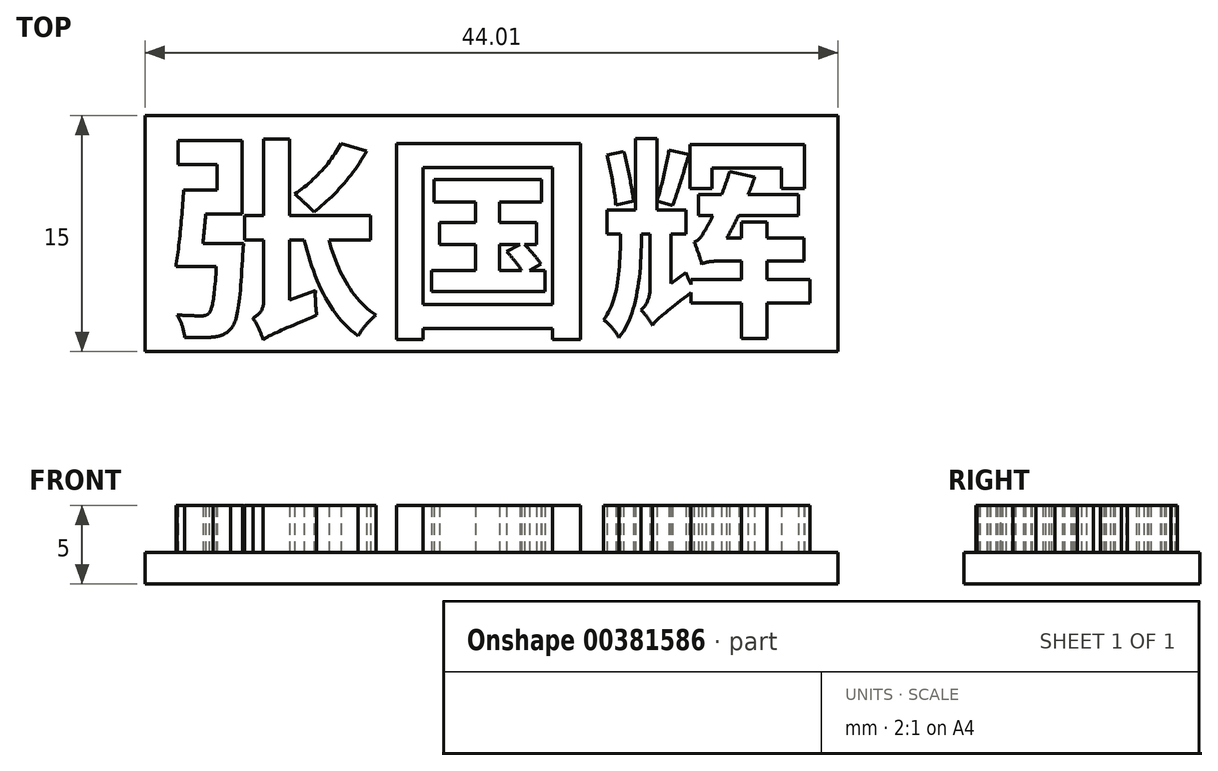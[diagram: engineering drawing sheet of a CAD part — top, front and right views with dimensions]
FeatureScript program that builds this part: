
annotation { "Feature Type Name" : "Feature", "Feature Type Description" : "" }
export const myFeature = defineFeature(function(context is Context, id is Id, definition is map)
    precondition{}
    {
        {
            var Q0;
            Q0=qCreatedBy(makeId("Top.planeOp"),FACE);
            var sketch = newSketch(context, id + "F0", { "sketchPlane" : qUnion([Q0])});
            skText(sketch, "E0", { "text": "张国辉", "fontName": "NotoSansCJKsc-Bold.otf"});
            skLineSegment(sketch, "E1.bottom", {"start": v(-1, 13) * mm, "end": v(43, 13) * mm});
            skLineSegment(sketch, "E1.top", {"start": v(-1, -2) * mm, "end": v(43, -2) * mm});
            skLineSegment(sketch, "E1.left", {"start": v(-1, 13) * mm, "end": v(-1, -2) * mm});
            skLineSegment(sketch, "E1.right", {"start": v(43, 13) * mm, "end": v(43, -2) * mm});
            const initialGuessF0  = {"E0": [0, 0, 1, 0, 0.01]};
            skSetInitialGuess(sketch, initialGuessF0);
            skSolve(sketch);
        }
        {
            var Q0;
            Q0=makeQuery(id+"F0.imprint","IMPRINT",FACE,{"disambiguationData":[TD([[makeQuery(id+"F0.imprint","IMPRINT",EDGE,{"derivedFrom":sQuery(id+"F0.wireOp",EDGE,"E0.sketch_text.stroke-0")}),-1.0]])]});
            var Q1;
            Q1=makeQuery(id+"F0.imprint","IMPRINT",FACE,{"disambiguationData":[TD([[makeQuery(id+"F0.imprint","IMPRINT",EDGE,{"derivedFrom":sQuery(id+"F0.wireOp",EDGE,"E0.sketch_text.stroke-0")}),1.0]])]});
            var Q2;
            Q2=makeQuery(id+"F0.imprint","IMPRINT",FACE,{"disambiguationData":[TD([[makeQuery(id+"F0.imprint","IMPRINT",EDGE,{"derivedFrom":sQuery(id+"F0.wireOp",EDGE,"E0.sketch_text.stroke-19")}),1.0]])]});
            var Q3;
            Q3=makeQuery(id+"F0.imprint","IMPRINT",FACE,{"disambiguationData":[TD([[makeQuery(id+"F0.imprint","IMPRINT",EDGE,{"derivedFrom":sQuery(id+"F0.wireOp",EDGE,"E0.sketch_text.stroke-45")}),1.0]])]});
            var Q4;
            Q4=makeQuery(id+"F0.imprint","IMPRINT",FACE,{"disambiguationData":[TD([[makeQuery(id+"F0.imprint","IMPRINT",EDGE,{"derivedFrom":sQuery(id+"F0.wireOp",EDGE,"E0.sketch_text.stroke-41")}),1.0]])]});
            var Q5;
            Q5=makeQuery(id+"F0.imprint","IMPRINT",FACE,{"disambiguationData":[TD([[makeQuery(id+"F0.imprint","IMPRINT",EDGE,{"derivedFrom":sQuery(id+"F0.wireOp",EDGE,"E0.sketch_text.stroke-37")}),1.0]])]});
            var Q6;
            Q6=makeQuery(id+"F0.imprint","IMPRINT",FACE,{"disambiguationData":[TD([[makeQuery(id+"F0.imprint","IMPRINT",EDGE,{"derivedFrom":sQuery(id+"F0.wireOp",EDGE,"E0.sketch_text.stroke-69")}),1.0]])]});
            var Q7;
            Q7=makeQuery(id+"F0.imprint","IMPRINT",FACE,{"disambiguationData":[TD([[makeQuery(id+"F0.imprint","IMPRINT",EDGE,{"derivedFrom":sQuery(id+"F0.wireOp",EDGE,"E0.sketch_text.stroke-69")}),-1.0]])]});
            var Q8;
            Q8=makeQuery(id+"F0.imprint","IMPRINT",FACE,{"disambiguationData":[TD([[makeQuery(id+"F0.imprint","IMPRINT",EDGE,{"derivedFrom":sQuery(id+"F0.wireOp",EDGE,"E0.sketch_text.stroke-49")}),1.0]])]});
            var Q9;
            Q9=makeQuery(id+"F0.imprint","IMPRINT",FACE,{"disambiguationData":[TD([[makeQuery(id+"F0.imprint","IMPRINT",EDGE,{"derivedFrom":sQuery(id+"F0.wireOp",EDGE,"E0.sketch_text.stroke-85")}),1.0]])]});
            var Q10;
            Q10=makeQuery(id+"F0.imprint","IMPRINT",FACE,{"disambiguationData":[TD([[makeQuery(id+"F0.imprint","IMPRINT",EDGE,{"derivedFrom":sQuery(id+"F0.wireOp",EDGE,"E0.sketch_text.stroke-85")}),-1.0]])]});
            var Q11;
            Q11=makeQuery(id+"F0.imprint","IMPRINT",FACE,{"disambiguationData":[TD([[makeQuery(id+"F0.imprint","IMPRINT",EDGE,{"derivedFrom":sQuery(id+"F0.wireOp",EDGE,"E0.sketch_text.stroke-138")}),1.0]])]});
            var Q12;
            Q12=makeQuery(id+"F0.imprint","IMPRINT",FACE,{"disambiguationData":[TD([[makeQuery(id+"F0.imprint","IMPRINT",EDGE,{"derivedFrom":sQuery(id+"F0.wireOp",EDGE,"E0.sketch_text.stroke-142")}),1.0]])]});
            var Q13;
            Q13=makeQuery(id+"F0.imprint","IMPRINT",FACE,{"disambiguationData":[TD([[makeQuery(id+"F0.imprint","IMPRINT",EDGE,{"derivedFrom":sQuery(id+"F0.wireOp",EDGE,"E0.sketch_text.stroke-89")}),1.0]])]});
            var Q14;
            Q14=makeQuery(id+"F0.imprint","IMPRINT",FACE,{"disambiguationData":[TD([[makeQuery(id+"F0.imprint","IMPRINT",EDGE,{"derivedFrom":sQuery(id+"F0.wireOp",EDGE,"E0.sketch_text.stroke-43")}),-1.0]])]});
            extrude(context, id + "F1", {"entities" : qUnion([Q0, Q1, Q2, Q3, Q4, Q5, Q6, Q7, Q8, Q9, Q10, Q11, Q12, Q13, Q14]), "oppositeDirection" : true, "depth" : 2 * mm, "offsetDistance" : 25 * mm});
        }
        {
            var Q0;
            Q0=makeQuery(id+"F0.imprint","IMPRINT",FACE,{"disambiguationData":[TD([[makeQuery(id+"F0.imprint","IMPRINT",EDGE,{"derivedFrom":sQuery(id+"F0.wireOp",EDGE,"E0.sketch_text.stroke-0")}),1.0]])]});
            var Q1;
            Q1=makeQuery(id+"F0.imprint","IMPRINT",FACE,{"disambiguationData":[TD([[makeQuery(id+"F0.imprint","IMPRINT",EDGE,{"derivedFrom":sQuery(id+"F0.wireOp",EDGE,"E0.sketch_text.stroke-19")}),1.0]])]});
            var Q2;
            Q2=makeQuery(id+"F0.imprint","IMPRINT",FACE,{"disambiguationData":[TD([[makeQuery(id+"F0.imprint","IMPRINT",EDGE,{"derivedFrom":sQuery(id+"F0.wireOp",EDGE,"E0.sketch_text.stroke-69")}),1.0]])]});
            var Q3;
            Q3=makeQuery(id+"F0.imprint","IMPRINT",FACE,{"disambiguationData":[TD([[makeQuery(id+"F0.imprint","IMPRINT",EDGE,{"derivedFrom":sQuery(id+"F0.wireOp",EDGE,"E0.sketch_text.stroke-37")}),1.0]])]});
            var Q4;
            Q4=makeQuery(id+"F0.imprint","IMPRINT",FACE,{"disambiguationData":[TD([[makeQuery(id+"F0.imprint","IMPRINT",EDGE,{"derivedFrom":sQuery(id+"F0.wireOp",EDGE,"E0.sketch_text.stroke-41")}),1.0]])]});
            var Q5;
            Q5=makeQuery(id+"F0.imprint","IMPRINT",FACE,{"disambiguationData":[TD([[makeQuery(id+"F0.imprint","IMPRINT",EDGE,{"derivedFrom":sQuery(id+"F0.wireOp",EDGE,"E0.sketch_text.stroke-45")}),1.0]])]});
            var Q6;
            Q6=makeQuery(id+"F0.imprint","IMPRINT",FACE,{"disambiguationData":[TD([[makeQuery(id+"F0.imprint","IMPRINT",EDGE,{"derivedFrom":sQuery(id+"F0.wireOp",EDGE,"E0.sketch_text.stroke-49")}),1.0]])]});
            var Q7;
            Q7=makeQuery(id+"F0.imprint","IMPRINT",FACE,{"disambiguationData":[TD([[makeQuery(id+"F0.imprint","IMPRINT",EDGE,{"derivedFrom":sQuery(id+"F0.wireOp",EDGE,"E0.sketch_text.stroke-138")}),1.0]])]});
            var Q8;
            Q8=makeQuery(id+"F0.imprint","IMPRINT",FACE,{"disambiguationData":[TD([[makeQuery(id+"F0.imprint","IMPRINT",EDGE,{"derivedFrom":sQuery(id+"F0.wireOp",EDGE,"E0.sketch_text.stroke-85")}),1.0]])]});
            var Q9;
            Q9=makeQuery(id+"F0.imprint","IMPRINT",FACE,{"disambiguationData":[TD([[makeQuery(id+"F0.imprint","IMPRINT",EDGE,{"derivedFrom":sQuery(id+"F0.wireOp",EDGE,"E0.sketch_text.stroke-142")}),1.0]])]});
            var Q10;
            Q10=makeQuery(id+"F0.imprint","IMPRINT",FACE,{"disambiguationData":[TD([[makeQuery(id+"F0.imprint","IMPRINT",EDGE,{"derivedFrom":sQuery(id+"F0.wireOp",EDGE,"E0.sketch_text.stroke-89")}),1.0]])]});
            extrude(context, id + "F2", {"entities" : qUnion([Q0, Q1, Q2, Q3, Q4, Q5, Q6, Q7, Q8, Q9, Q10]), "operationType" : NewBodyOperationType.ADD, "depth" : 3 * mm, "offsetDistance" : 25 * mm});
        }
    });
